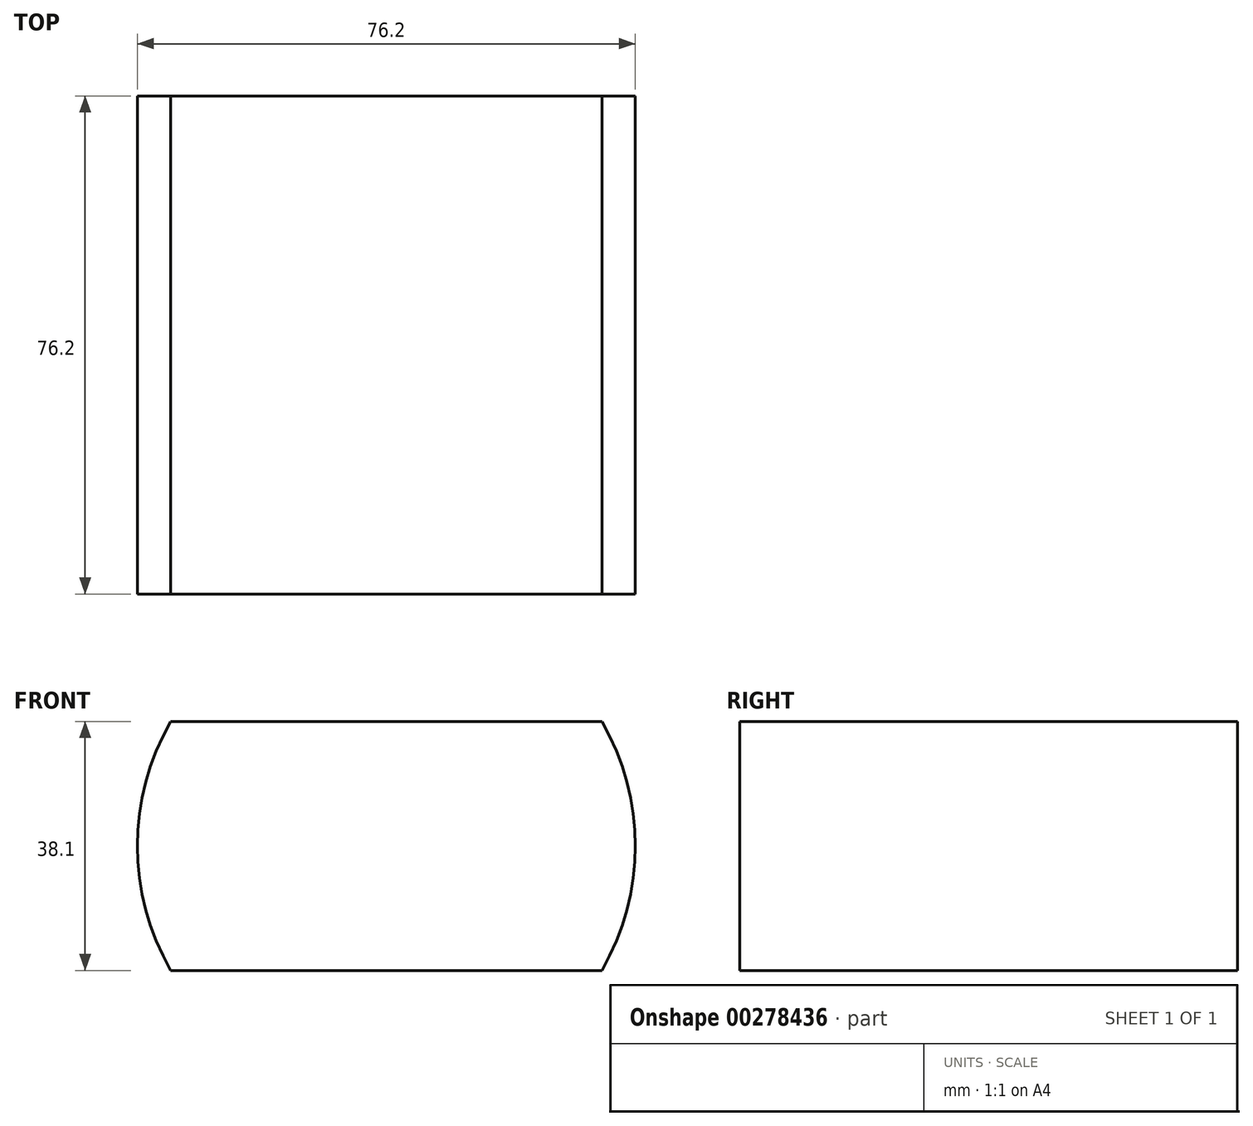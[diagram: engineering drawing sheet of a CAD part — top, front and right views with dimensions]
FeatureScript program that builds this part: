
annotation { "Feature Type Name" : "Feature", "Feature Type Description" : "" }
export const myFeature = defineFeature(function(context is Context, id is Id, definition is map)
    precondition{}
    {
        {
            var Q0;
            Q0=qCreatedBy(makeId("Front.planeOp"),FACE);
            var sketch = newSketch(context, id + "F0", { "sketchPlane" : qUnion([Q0])});
            skCircle(sketch, "E0", {"center": v(0, 0) * mm, "radius": 38.1 * mm});
            skSolve(sketch);
        }
        {
            var Q0;
            Q0=makeQuery(id+"F0.imprint","IMPRINT",FACE,{"disambiguationData":[TD([[makeQuery(id+"F0.imprint","IMPRINT",EDGE,{"derivedFrom":sQuery(id+"F0.wireOp",EDGE,"E0")}),1.0]])]});
            extrude(context, id + "F1", {"entities" : qUnion([Q0]), "depth" : 127 * mm});
        }
        {
            var Q0;
            Q0=qCreatedBy(makeId("Front.planeOp"),FACE);
            cPlane(context, id + "F2", {"entities" : qUnion([Q0]), "cplaneType" : CPlaneType.OFFSET, "offset" : 63.5 * mm, "width" : 152.4 * mm, "height" : 152.4 * mm});
        }
        {
            var Q0;
            Q0=qCreatedBy(makeId("Right.planeOp"),FACE);
            var sketch = newSketch(context, id + "F3", { "sketchPlane" : qUnion([Q0])});
            skLineSegment(sketch, "E1.bottom", {"start": v(-36.1, -19.05) * mm, "end": v(-112.3, -19.05) * mm});
            skLineSegment(sketch, "E1.top", {"start": v(-36.1, 19.05) * mm, "end": v(-112.3, 19.05) * mm});
            skLineSegment(sketch, "E1.left", {"start": v(-36.1, -19.05) * mm, "end": v(-36.1, 19.05) * mm});
            skLineSegment(sketch, "E1.right", {"start": v(-112.3, -19.05) * mm, "end": v(-112.3, 19.05) * mm});
            skPoint(sketch, "E1.middle", {"position": v(-74.2, 0) * mm});
            skSolve(sketch);
        }
        {
            var Q0;
            Q0 = qSketchRegion(id + "F3", true);
            extrude(context, id + "F4", {"entities" : qUnion([Q0]), "operationType" : NewBodyOperationType.INTERSECT, "endBound" : BoundingType.SYMMETRIC, "depth" : 203.2 * mm});
        }
    });
